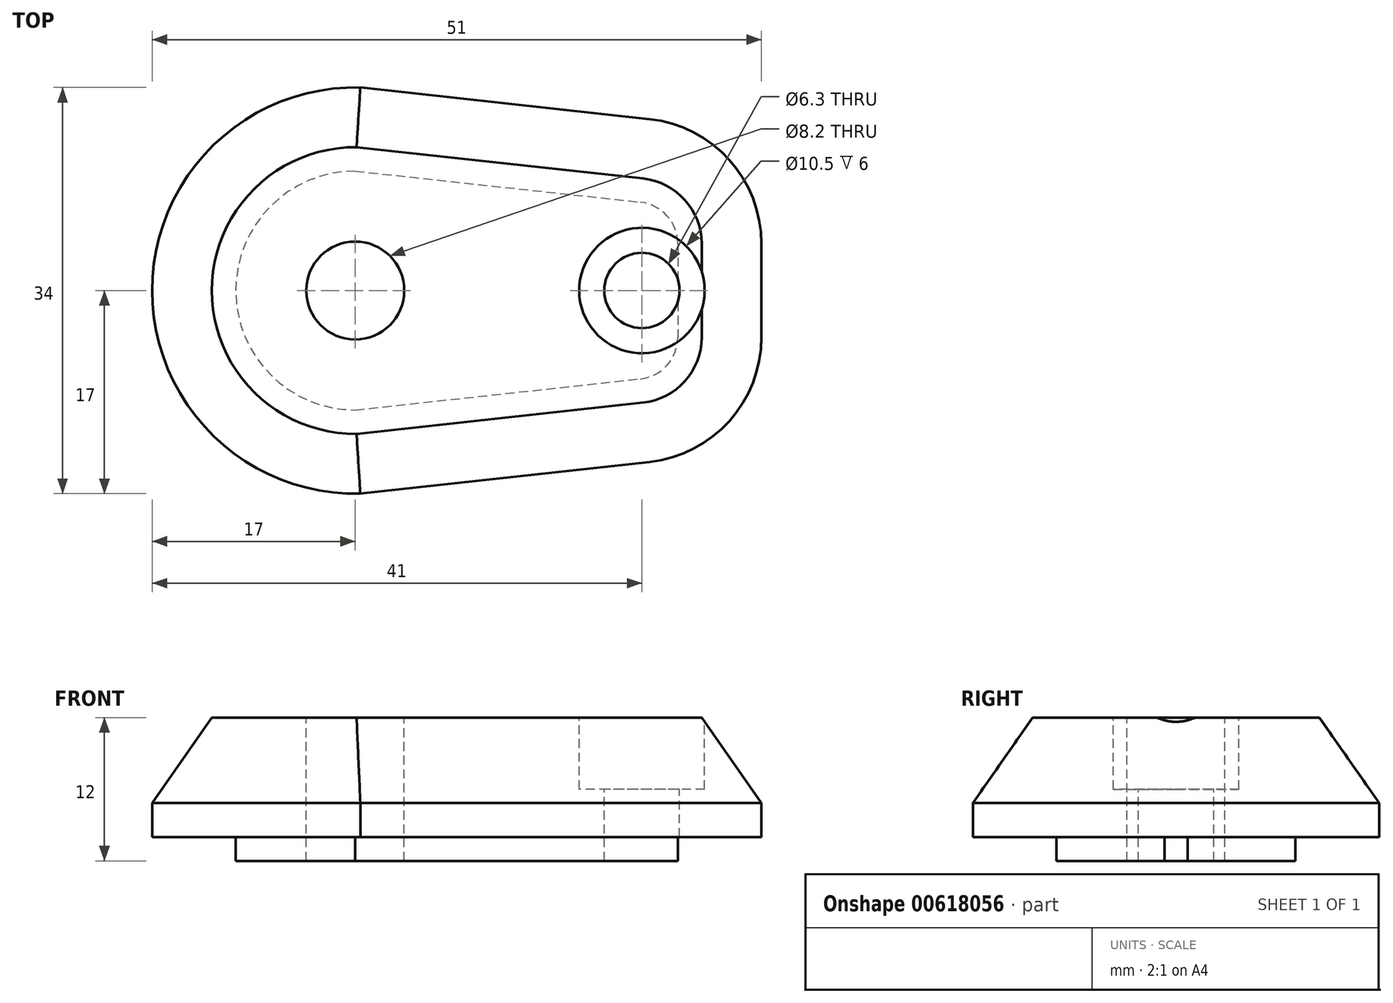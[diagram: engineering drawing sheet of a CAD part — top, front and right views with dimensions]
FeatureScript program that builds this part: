
annotation { "Feature Type Name" : "Feature", "Feature Type Description" : "" }
export const myFeature = defineFeature(function(context is Context, id is Id, definition is map)
    precondition{}
    {
        {
            var Q0;
            Q0=qCreatedBy(makeId("Top.planeOp"),FACE);
            var sketch = newSketch(context, id + "F0", { "sketchPlane" : qUnion([Q0])});
            skArc(sketch, "E0", {"start": v(2.16, 9.76) * mm, "mid": v(-10, 0) * mm, "end": v(2.16, -9.76) * mm});
            skLineSegment(sketch, "E1", {"start": v(27, 3.92) * mm, "end": v(27, -3.92) * mm});
            skLineSegment(sketch, "E2", {"start": v(0, 10) * mm, "end": v(23.88, 7.4) * mm});
            skLineSegment(sketch, "E3", {"start": v(0, -10) * mm, "end": v(23.88, -7.4) * mm});
            skPoint(sketch, "E4.newPointB", {"position": v(27.5, 7) * mm});
            skArc(sketch, "E4.filletArc", {"start": v(27, 3.92) * mm, "mid": v(26.1, 6.25) * mm, "end": v(23.88, 7.4) * mm});
            skPoint(sketch, "E5.newPointA", {"position": v(27.5, -7) * mm});
            skArc(sketch, "E5.filletArc", {"start": v(23.88, -7.4) * mm, "mid": v(26.1, -6.25) * mm, "end": v(27, -3.92) * mm});
            skSolve(sketch);
        }
        {
            var Q0;
            Q0=makeQuery(id+"F0.imprint","IMPRINT",FACE,{"disambiguationData":[TD([[makeQuery(id+"F0.imprint","IMPRINT",EDGE,{"derivedFrom":sQuery(id+"F0.wireOp",EDGE,"E1")}),-1.0]])]});
            extrude(context, id + "F1", {"entities" : qUnion([Q0]), "depth" : 2 * mm, "offsetDistance" : 25 * mm});
        }
        {
            var Q0;
            Q0=makeQuery(id+"F1.opExtrude","CAP_FACE",FACE,{"disambiguationData":[OSD([sQuery(id+"F0.wireOp",EDGE,"E0"),sQuery(id+"F0.wireOp",EDGE,"E1"),sQuery(id+"F0.wireOp",EDGE,"E2"),sQuery(id+"F0.wireOp",EDGE,"E3"),sQuery(id+"F0.wireOp",EDGE,"E4.filletArc"),sQuery(id+"F0.wireOp",EDGE,"E5.filletArc")])],"isStart":false});
            var sketch = newSketch(context, id + "F2", { "sketchPlane" : qUnion([Q0])});
            skLineSegment(sketch, "E6.0", {"start": v(0.43, 17) * mm, "end": v(24.64, 14.35) * mm});
            skLineSegment(sketch, "E6.1", {"start": v(0.43, -17) * mm, "end": v(24.64, -14.35) * mm});
            skArc(sketch, "E6.2", {"start": v(24.64, -14.35) * mm, "mid": v(31.32, -10.93) * mm, "end": v(34, -3.92) * mm});
            skArc(sketch, "E6.3", {"start": v(0.43, 17) * mm, "mid": v(-17, 0) * mm, "end": v(0.43, -17) * mm});
            skLineSegment(sketch, "E6.4", {"start": v(34, 3.92) * mm, "end": v(34, -3.92) * mm});
            skArc(sketch, "E6.5", {"start": v(34, 3.92) * mm, "mid": v(31.32, 10.93) * mm, "end": v(24.64, 14.35) * mm});
            skSolve(sketch);
        }
        {
            var Q0;
            Q0=makeQuery(id+"F2.imprint","IMPRINT",FACE,{"disambiguationData":[TD([[makeQuery(id+"F2.imprint","IMPRINT",EDGE,{"derivedFrom":sQuery(id+"F2.wireOp",EDGE,"E6.0")}),-1.0]])]});
            var Q1;
            Q1 = qSketchRegion(id + "F2", true);
            extrude(context, id + "F3", {"entities" : qUnion([Q0, Q1]), "operationType" : NewBodyOperationType.ADD, "depth" : 10 * mm, "offsetDistance" : 25 * mm});
        }
        {
            var Q0;
            Q0=makeQuery(id+"F3.opExtrude","CAP_FACE",FACE,{"disambiguationData":[OSD([sQuery(id+"F2.wireOp",EDGE,"E6.0"),sQuery(id+"F2.wireOp",EDGE,"E6.1"),sQuery(id+"F2.wireOp",EDGE,"E6.2"),sQuery(id+"F2.wireOp",EDGE,"E6.3"),sQuery(id+"F2.wireOp",EDGE,"E6.4"),sQuery(id+"F2.wireOp",EDGE,"E6.5")])],"isStart":false});
            var sketch = newSketch(context, id + "F4", { "sketchPlane" : qUnion([Q0])});
            skCircle(sketch, "E7", {"center": v(0, 0) * mm, "radius": 4.1 * mm});
            skCircle(sketch, "E8", {"center": v(24, 0) * mm, "radius": 3.15 * mm});
            skSolve(sketch);
        }
        {
            var Q0;
            Q0=makeQuery(id+"F4.imprint","IMPRINT",FACE,{"disambiguationData":[TD([[makeQuery(id+"F4.imprint","IMPRINT",EDGE,{"derivedFrom":sQuery(id+"F4.wireOp",EDGE,"E7")}),1.0]])]});
            var Q1;
            Q1=makeQuery(id+"F4.imprint","IMPRINT",FACE,{"disambiguationData":[TD([[makeQuery(id+"F4.imprint","IMPRINT",EDGE,{"derivedFrom":sQuery(id+"F4.wireOp",EDGE,"E8")}),1.0]])]});
            extrude(context, id + "F5", {"entities" : qUnion([Q0, Q1]), "operationType" : NewBodyOperationType.REMOVE, "oppositeDirection" : true, "depth" : 25 * mm, "offsetDistance" : 25 * mm});
        }
        {
            var Q0;
            Q0=makeQuery(id+"F3.opExtrude","CAP_FACE",FACE,{"disambiguationData":[OSD([sQuery(id+"F2.wireOp",EDGE,"E6.0"),sQuery(id+"F2.wireOp",EDGE,"E6.1"),sQuery(id+"F2.wireOp",EDGE,"E6.2"),sQuery(id+"F2.wireOp",EDGE,"E6.3"),sQuery(id+"F2.wireOp",EDGE,"E6.4"),sQuery(id+"F2.wireOp",EDGE,"E6.5")])],"isStart":false});
            var sketch = newSketch(context, id + "F6", { "sketchPlane" : qUnion([Q0])});
            skCircle(sketch, "E9", {"center": v(24, 0) * mm, "radius": 5.25 * mm});
            skSolve(sketch);
        }
        {
            var Q0;
            Q0=makeQuery(id+"F6.imprint","IMPRINT",FACE,{"disambiguationData":[TD([[makeQuery(id+"F6.imprint","IMPRINT",EDGE,{"derivedFrom":sQuery(id+"F6.wireOp",EDGE,"E9")}),1.0]])]});
            extrude(context, id + "F7", {"entities" : qUnion([Q0]), "operationType" : NewBodyOperationType.REMOVE, "oppositeDirection" : true, "depth" : 6 * mm, "offsetDistance" : 25 * mm});
        }
        {
            var Q0;
            Q0=makeQuery(id+"F3.opExtrude","CAP_EDGE",EDGE,{"disambiguationData":[OSD([sQuery(id+"F2.wireOp",EDGE,"E6.3")])],"isStart":false});
            var Q1;
            Q1=makeQuery(id+"F3.opExtrude","CAP_EDGE",EDGE,{"disambiguationData":[OSD([sQuery(id+"F2.wireOp",EDGE,"E6.1")])],"isStart":false});
            var Q2;
            Q2=makeQuery(id+"F3.opExtrude","CAP_EDGE",EDGE,{"disambiguationData":[OSD([sQuery(id+"F2.wireOp",EDGE,"E6.2")])],"isStart":false});
            var Q3;
            Q3=makeQuery(id+"F3.opExtrude","CAP_EDGE",EDGE,{"disambiguationData":[OSD([sQuery(id+"F2.wireOp",EDGE,"E6.4")])],"isStart":false});
            var Q4;
            Q4=makeQuery(id+"F3.opExtrude","CAP_EDGE",EDGE,{"disambiguationData":[OSD([sQuery(id+"F2.wireOp",EDGE,"E6.5")])],"isStart":false});
            var Q5;
            Q5=makeQuery(id+"F3.opExtrude","CAP_EDGE",EDGE,{"disambiguationData":[OSD([sQuery(id+"F2.wireOp",EDGE,"E6.0")])],"isStart":false});
            chamfer(context, id + "F8", {"entities" : qUnion([Q0, Q1, Q2, Q3, Q4, Q5]), "chamferType" : ChamferType.OFFSET_ANGLE, "width" : 5 * mm, "oppositeDirection" : false, "angle" : 55 * degree, "tangentPropagation" : true});
        }
    });
